# Revit family: SWING - SINGLE FLUSH
name_source: partatom
category: Doors
revit_build: Autodesk Revit 2014 (Build: 20140709_2115(x64)
units: mm (PartAtom-declared; Revit-internal decimal feet)

## types (2) — shared parameters
Analytic Construction = <None>
Assembly Code = C1020
Function = Interior
RABBIT DEPTH = 0' - 1"
RABBIT WIDTH = 0' - 0 1/2"
SHOW TRIM = No
Wall Closure = By host

## per-type parameters (varying)
| type | DOOR TRIM DEPTH | DOOR TRIM WIDTH | Hardware Height | Hardware Offset | Height | JAMB WIDTH | PANEL CENTER (FRONT/BACK) | PANEL CENTER LOCATION | Thickness | Trim Projection Ext | Trim Projection Int | Trim Width | Width |
| 1000 X 2100 | 0' - 1" | 0' - 1" | 3' - 3" | 0' - 4" | 7' - 0" | 0' - 2" | 0' - 2 1/8" | 0' - 0 1/8" | 0' - 1 3/4" | 0' - 1" | 0' - 1" | 0' - 3" | 3' - 0" |
| 900 X 2100 | 0' - 0 63/64" | 0' - 0 63/64" | 3' - 2" | 0' - 3 15/16" | 6' - 10 173/256" | 0' - 1 31/32" | 0' - 1 31/32" | 0' - 0 63/64" | 0' - 1 99/128" | 0' - 0 63/64" | 0' - 0 63/64" | 0' - 2 61/64" | 2' - 11 111/256" |

## geometry (parser evidence)
native form markers: Sweep x7
no freeform markers — native parametric forms only
